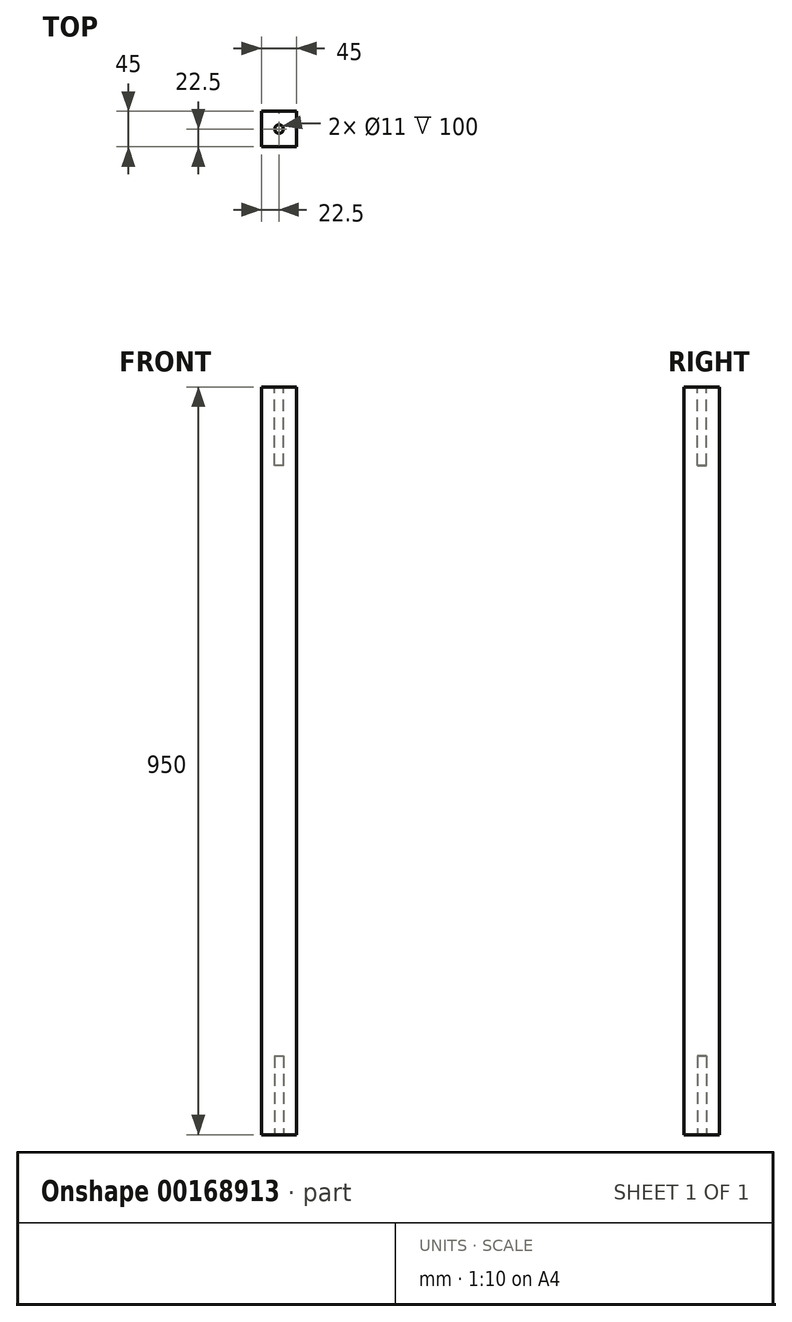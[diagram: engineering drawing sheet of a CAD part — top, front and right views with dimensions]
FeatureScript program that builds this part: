
annotation { "Feature Type Name" : "Feature", "Feature Type Description" : "" }
export const myFeature = defineFeature(function(context is Context, id is Id, definition is map)
    precondition{}
    {
        {
            var Q0;
            Q0=qCreatedBy(makeId("Top.planeOp"),FACE);
            var sketch = newSketch(context, id + "F0", { "sketchPlane" : qUnion([Q0])});
            skLineSegment(sketch, "E0.bottom", {"start": v(22.5, 22.5) * mm, "end": v(-22.5, 22.5) * mm});
            skLineSegment(sketch, "E0.top", {"start": v(22.5, -22.5) * mm, "end": v(-22.5, -22.5) * mm});
            skLineSegment(sketch, "E0.left", {"start": v(22.5, 22.5) * mm, "end": v(22.5, -22.5) * mm});
            skLineSegment(sketch, "E0.right", {"start": v(-22.5, 22.5) * mm, "end": v(-22.5, -22.5) * mm});
            skPoint(sketch, "E0.middle", {"position": v(0, 0) * mm});
            skSolve(sketch);
        }
        {
            var Q0;
            Q0=makeQuery(id+"F0.imprint","IMPRINT",FACE,{"disambiguationData":[TD([[makeQuery(id+"F0.imprint","IMPRINT",EDGE,{"derivedFrom":sQuery(id+"F0.wireOp",EDGE,"E0.bottom")}),1.0]])]});
            extrude(context, id + "F1", {"entities" : qUnion([Q0]), "depth" : 950 * mm});
        }
        {
            var Q0;
            Q0=makeQuery(id+"F1.opExtrude","CAP_FACE",FACE,{"disambiguationData":[OSD([sQuery(id+"F0.wireOp",EDGE,"E0.bottom"),sQuery(id+"F0.wireOp",EDGE,"E0.top"),sQuery(id+"F0.wireOp",EDGE,"E0.left"),sQuery(id+"F0.wireOp",EDGE,"E0.right")])],"isStart":false});
            var sketch = newSketch(context, id + "F2", { "sketchPlane" : qUnion([Q0])});
            skCircle(sketch, "E1", {"center": v(0, 0) * mm, "radius": 5.5 * mm});
            skSolve(sketch);
        }
        {
            var Q0;
            Q0=makeQuery(id+"F1.opExtrude","CAP_FACE",FACE,{"disambiguationData":[OSD([sQuery(id+"F0.wireOp",EDGE,"E0.bottom"),sQuery(id+"F0.wireOp",EDGE,"E0.top"),sQuery(id+"F0.wireOp",EDGE,"E0.left"),sQuery(id+"F0.wireOp",EDGE,"E0.right")])],"isStart":true});
            var sketch = newSketch(context, id + "F3", { "sketchPlane" : qUnion([Q0])});
            skCircle(sketch, "E2", {"center": v(0, 0) * mm, "radius": 5.5 * mm});
            skSolve(sketch);
        }
        {
            var Q0;
            Q0=makeQuery(id+"F3.imprint","IMPRINT",FACE,{"disambiguationData":[TD([[makeQuery(id+"F3.imprint","IMPRINT",EDGE,{"derivedFrom":sQuery(id+"F3.wireOp",EDGE,"E2")}),1.0]])]});
            extrude(context, id + "F4", {"entities" : qUnion([Q0]), "operationType" : NewBodyOperationType.REMOVE, "oppositeDirection" : true, "depth" : 100 * mm});
        }
        {
            var Q0;
            Q0=makeQuery(id+"F2.imprint","IMPRINT",FACE,{"disambiguationData":[TD([[makeQuery(id+"F2.imprint","IMPRINT",EDGE,{"derivedFrom":sQuery(id+"F2.wireOp",EDGE,"E1")}),1.0]])]});
            extrude(context, id + "F5", {"entities" : qUnion([Q0]), "operationType" : NewBodyOperationType.REMOVE, "oppositeDirection" : true, "depth" : 100 * mm});
        }
    });
